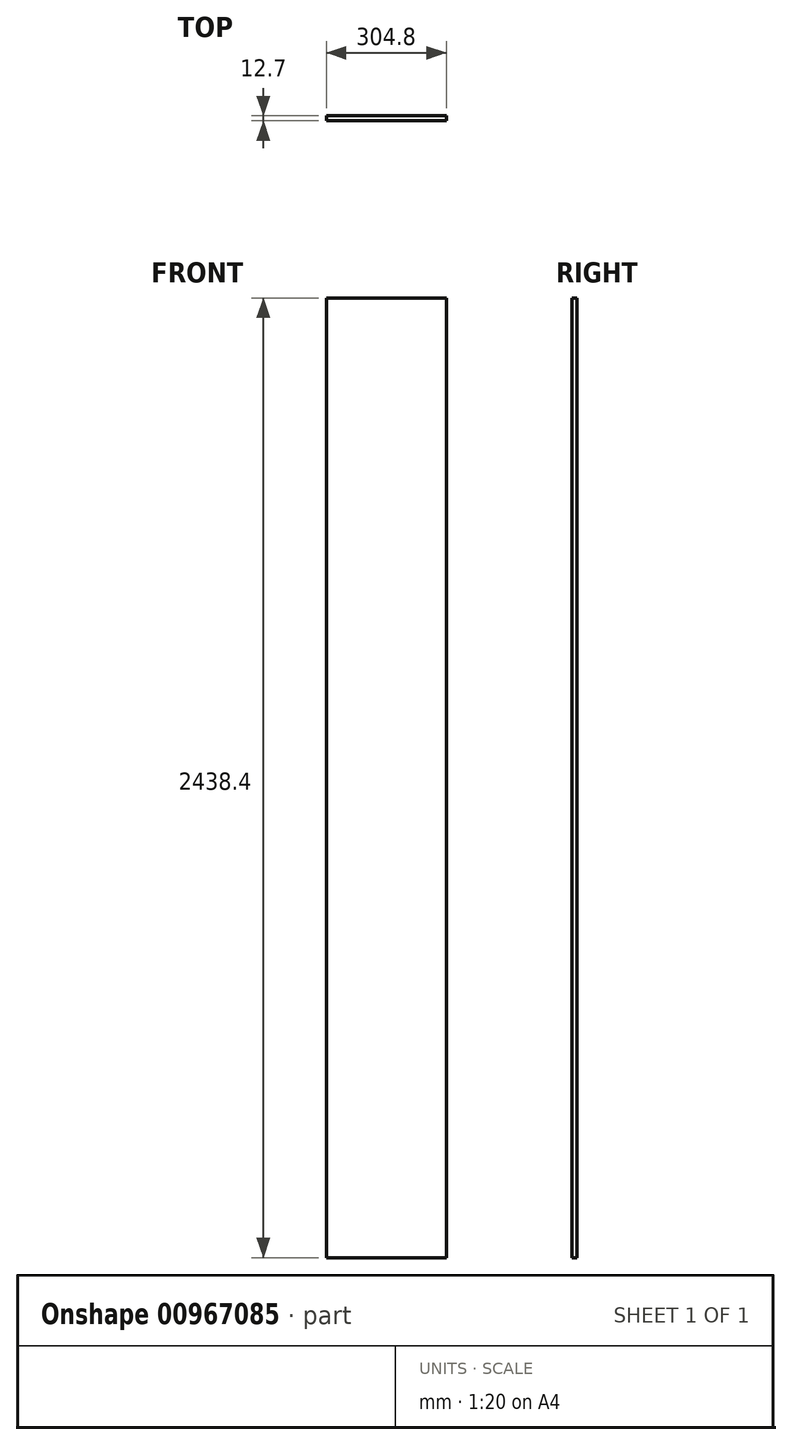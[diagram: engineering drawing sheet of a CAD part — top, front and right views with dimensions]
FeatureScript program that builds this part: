
annotation { "Feature Type Name" : "Feature", "Feature Type Description" : "" }
export const myFeature = defineFeature(function(context is Context, id is Id, definition is map)
    precondition{}
    {
        {
            var Q0;
            Q0=qCreatedBy(makeId("Front.planeOp"),FACE);
            var sketch = newSketch(context, id + "F0", { "sketchPlane" : qUnion([Q0])});
            skLineSegment(sketch, "E0.bottom", {"start": v(0, 0) * mm, "end": v(-304.8, 0) * mm});
            skLineSegment(sketch, "E0.top", {"start": v(0, 2438.4) * mm, "end": v(-304.8, 2438.4) * mm});
            skLineSegment(sketch, "E0.left", {"start": v(0, 0) * mm, "end": v(0, 2438.4) * mm});
            skLineSegment(sketch, "E0.right", {"start": v(-304.8, 0) * mm, "end": v(-304.8, 2438.4) * mm});
            skSolve(sketch);
        }
        {
            var Q0;
            Q0=makeQuery(id+"F0.imprint","IMPRINT",FACE,{"disambiguationData":[TD([[makeQuery(id+"F0.imprint","IMPRINT",EDGE,{"derivedFrom":sQuery(id+"F0.wireOp",EDGE,"E0.bottom")}),-1.0]])]});
            extrude(context, id + "F1", {"entities" : qUnion([Q0]), "depth" : 12.7 * mm, "offsetDistance" : 25.4 * mm});
        }
    });
